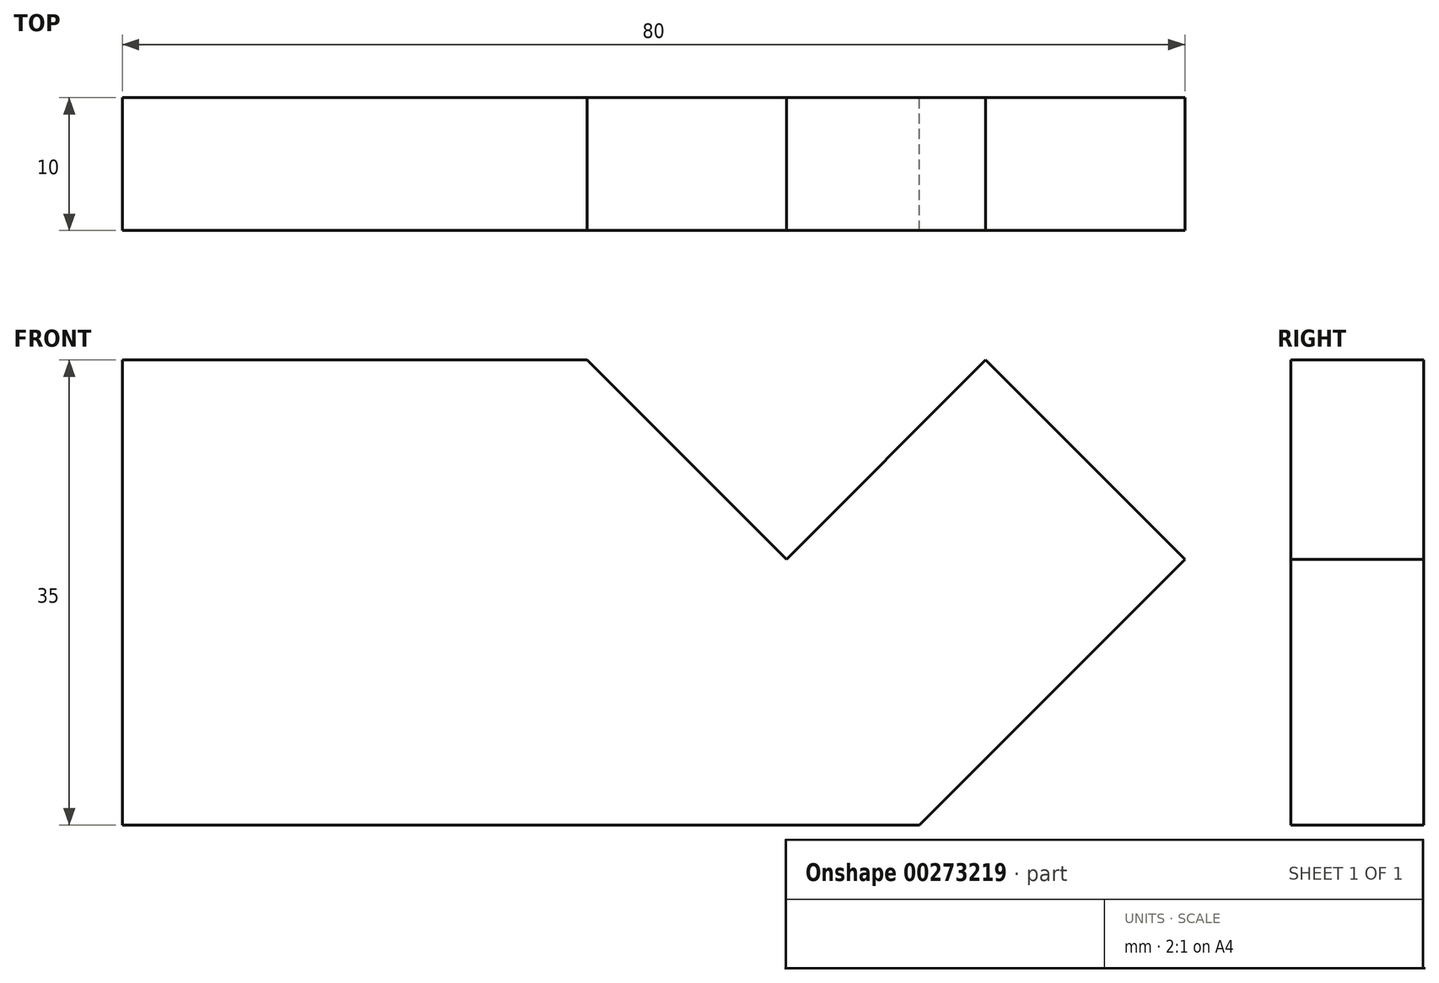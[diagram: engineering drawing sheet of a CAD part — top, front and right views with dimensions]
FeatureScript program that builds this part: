
annotation { "Feature Type Name" : "Feature", "Feature Type Description" : "" }
export const myFeature = defineFeature(function(context is Context, id is Id, definition is map)
    precondition{}
    {
        {
            var Q0;
            Q0=qCreatedBy(makeId("Front.planeOp"),FACE);
            var sketch = newSketch(context, id + "F0", { "sketchPlane" : qUnion([Q0])});
            skLineSegment(sketch, "E0", {"start": v(0, 0) * mm, "end": v(0, 35) * mm});
            skLineSegment(sketch, "E1", {"start": v(50, 20) * mm, "end": v(35, 35) * mm});
            skLineSegment(sketch, "E2", {"start": v(0, 35) * mm, "end": v(35, 35) * mm});
            skLineSegment(sketch, "E3", {"start": v(50, 20) * mm, "end": v(65, 35) * mm});
            skLineSegment(sketch, "E4", {"start": v(0, 0) * mm, "end": v(60, 0) * mm});
            skLineSegment(sketch, "E5", {"start": v(65, 35) * mm, "end": v(80, 20) * mm});
            skLineSegment(sketch, "E6", {"start": v(80, 20) * mm, "end": v(60, 0) * mm});
            skSolve(sketch);
        }
        {
            var Q0;
            Q0 = qSketchRegion(id + "F0", true);
            extrude(context, id + "F1", {"entities" : qUnion([Q0]), "depth" : 10 * mm});
        }
    });
